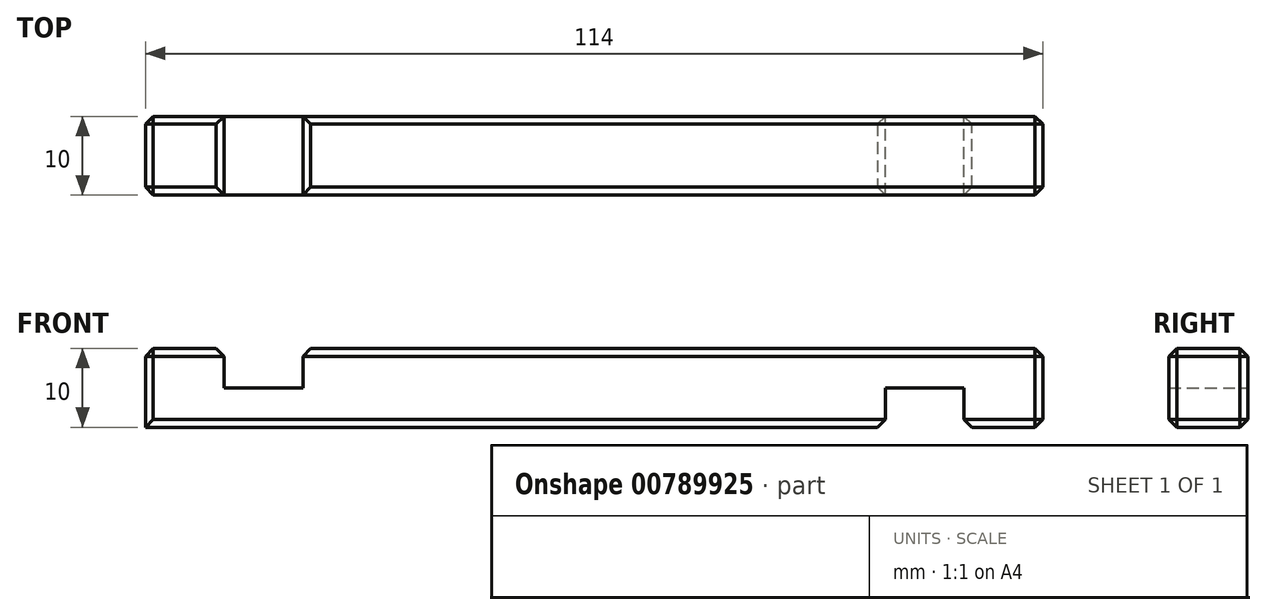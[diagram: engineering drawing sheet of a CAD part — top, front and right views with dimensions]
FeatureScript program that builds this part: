
annotation { "Feature Type Name" : "Feature", "Feature Type Description" : "" }
export const myFeature = defineFeature(function(context is Context, id is Id, definition is map)
    precondition{}
    {
        {
            var Q0;
            Q0=qCreatedBy(makeId("Front.planeOp"),FACE);
            var sketch = newSketch(context, id + "F0", { "sketchPlane" : qUnion([Q0])});
            skLineSegment(sketch, "E0", {"start": v(-57.43, 10) * mm, "end": v(-57.43, 0) * mm});
            skLineSegment(sketch, "E1", {"start": v(-57.43, 0) * mm, "end": v(36.57, 0) * mm});
            skLineSegment(sketch, "E2", {"start": v(36.57, 0) * mm, "end": v(36.57, 5) * mm});
            skLineSegment(sketch, "E3", {"start": v(36.57, 5) * mm, "end": v(46.57, 5) * mm});
            skLineSegment(sketch, "E4", {"start": v(46.57, 5) * mm, "end": v(46.57, 0) * mm});
            skLineSegment(sketch, "E5", {"start": v(46.57, 0) * mm, "end": v(56.57, 0) * mm});
            skLineSegment(sketch, "E6", {"start": v(56.57, 0) * mm, "end": v(56.57, 10) * mm});
            skLineSegment(sketch, "E7", {"start": v(56.57, 10) * mm, "end": v(-37.43, 10) * mm});
            skLineSegment(sketch, "E8", {"start": v(-37.43, 10) * mm, "end": v(-37.43, 5) * mm});
            skLineSegment(sketch, "E9", {"start": v(-37.43, 5) * mm, "end": v(-47.43, 5) * mm});
            skLineSegment(sketch, "E10", {"start": v(-47.43, 5) * mm, "end": v(-47.43, 10) * mm});
            skLineSegment(sketch, "E11", {"start": v(-47.43, 10) * mm, "end": v(-57.43, 10) * mm});
            skSolve(sketch);
        }
        {
            var Q0;
            Q0=makeQuery(id+"F0.imprint","IMPRINT",FACE,{"disambiguationData":[TD([[makeQuery(id+"F0.imprint","IMPRINT",EDGE,{"derivedFrom":sQuery(id+"F0.wireOp",EDGE,"E0")}),1.0]])]});
            extrude(context, id + "F1", {"entities" : qUnion([Q0]), "depth" : 10 * mm, "offsetDistance" : 25 * mm});
        }
        {
            var Q0;
            Q0=makeQuery(id+"F1.opExtrude","CAP_EDGE",EDGE,{"disambiguationData":[OSD([sQuery(id+"F0.wireOp",EDGE,"E11")])],"isStart":true});
            var Q1;
            Q1=makeQuery(id+"F1.opExtrude","SWEPT_EDGE",EDGE,{"disambiguationData":[OSD([sQuery(id+"F0.wireOp",EDGE,"E0"),sQuery(id+"F0.wireOp",EDGE,"E11")])]});
            var Q2;
            Q2=makeQuery(id+"F1.opExtrude","CAP_EDGE",EDGE,{"disambiguationData":[OSD([sQuery(id+"F0.wireOp",EDGE,"E11")])],"isStart":false});
            var Q3;
            Q3=makeQuery(id+"F1.opExtrude","CAP_EDGE",EDGE,{"disambiguationData":[OSD([sQuery(id+"F0.wireOp",EDGE,"E7")])],"isStart":true});
            var Q4;
            Q4=makeQuery(id+"F1.opExtrude","CAP_EDGE",EDGE,{"disambiguationData":[OSD([sQuery(id+"F0.wireOp",EDGE,"E7")])],"isStart":false});
            var Q5;
            Q5=makeQuery(id+"F1.opExtrude","SWEPT_EDGE",EDGE,{"disambiguationData":[OSD([sQuery(id+"F0.wireOp",EDGE,"E6"),sQuery(id+"F0.wireOp",EDGE,"E7")])]});
            var Q6;
            Q6=makeQuery(id+"F1.opExtrude","CAP_EDGE",EDGE,{"disambiguationData":[OSD([sQuery(id+"F0.wireOp",EDGE,"E0")])],"isStart":false});
            var Q7;
            Q7=makeQuery(id+"F1.opExtrude","CAP_EDGE",EDGE,{"disambiguationData":[OSD([sQuery(id+"F0.wireOp",EDGE,"E1")])],"isStart":false});
            var Q8;
            Q8=makeQuery(id+"F1.opExtrude","CAP_EDGE",EDGE,{"disambiguationData":[OSD([sQuery(id+"F0.wireOp",EDGE,"E5")])],"isStart":false});
            var Q9;
            Q9=makeQuery(id+"F1.opExtrude","CAP_EDGE",EDGE,{"disambiguationData":[OSD([sQuery(id+"F0.wireOp",EDGE,"E6")])],"isStart":false});
            var Q10;
            Q10=makeQuery(id+"F1.opExtrude","SWEPT_EDGE",EDGE,{"disambiguationData":[OSD([sQuery(id+"F0.wireOp",EDGE,"E5"),sQuery(id+"F0.wireOp",EDGE,"E6")])]});
            var Q11;
            Q11=makeQuery(id+"F1.opExtrude","CAP_EDGE",EDGE,{"disambiguationData":[OSD([sQuery(id+"F0.wireOp",EDGE,"E6")])],"isStart":true});
            var Q12;
            Q12=makeQuery(id+"F1.opExtrude","CAP_EDGE",EDGE,{"disambiguationData":[OSD([sQuery(id+"F0.wireOp",EDGE,"E5")])],"isStart":true});
            var Q13;
            Q13=makeQuery(id+"F1.opExtrude","CAP_EDGE",EDGE,{"disambiguationData":[OSD([sQuery(id+"F0.wireOp",EDGE,"E1")])],"isStart":true});
            var Q14;
            Q14=makeQuery(id+"F1.opExtrude","CAP_EDGE",EDGE,{"disambiguationData":[OSD([sQuery(id+"F0.wireOp",EDGE,"E0")])],"isStart":true});
            var Q15;
            Q15=makeQuery(id+"F1.opExtrude","SWEPT_EDGE",EDGE,{"disambiguationData":[OSD([sQuery(id+"F0.wireOp",EDGE,"E10"),sQuery(id+"F0.wireOp",EDGE,"E11")])]});
            var Q16;
            Q16=makeQuery(id+"F1.opExtrude","SWEPT_EDGE",EDGE,{"disambiguationData":[OSD([sQuery(id+"F0.wireOp",EDGE,"E7"),sQuery(id+"F0.wireOp",EDGE,"E8")])]});
            var Q17;
            Q17=makeQuery(id+"F1.opExtrude","SWEPT_EDGE",EDGE,{"disambiguationData":[OSD([sQuery(id+"F0.wireOp",EDGE,"E1"),sQuery(id+"F0.wireOp",EDGE,"E2")])]});
            var Q18;
            Q18=makeQuery(id+"F1.opExtrude","SWEPT_EDGE",EDGE,{"disambiguationData":[OSD([sQuery(id+"F0.wireOp",EDGE,"E4"),sQuery(id+"F0.wireOp",EDGE,"E5")])]});
            chamfer(context, id + "F2", {"entities" : qUnion([Q0, Q1, Q2, Q3, Q4, Q5, Q6, Q7, Q8, Q9, Q10, Q11, Q12, Q13, Q14, Q15, Q16, Q17, Q18]), "width" : 1 * mm, "tangentPropagation" : true});
        }
    });
